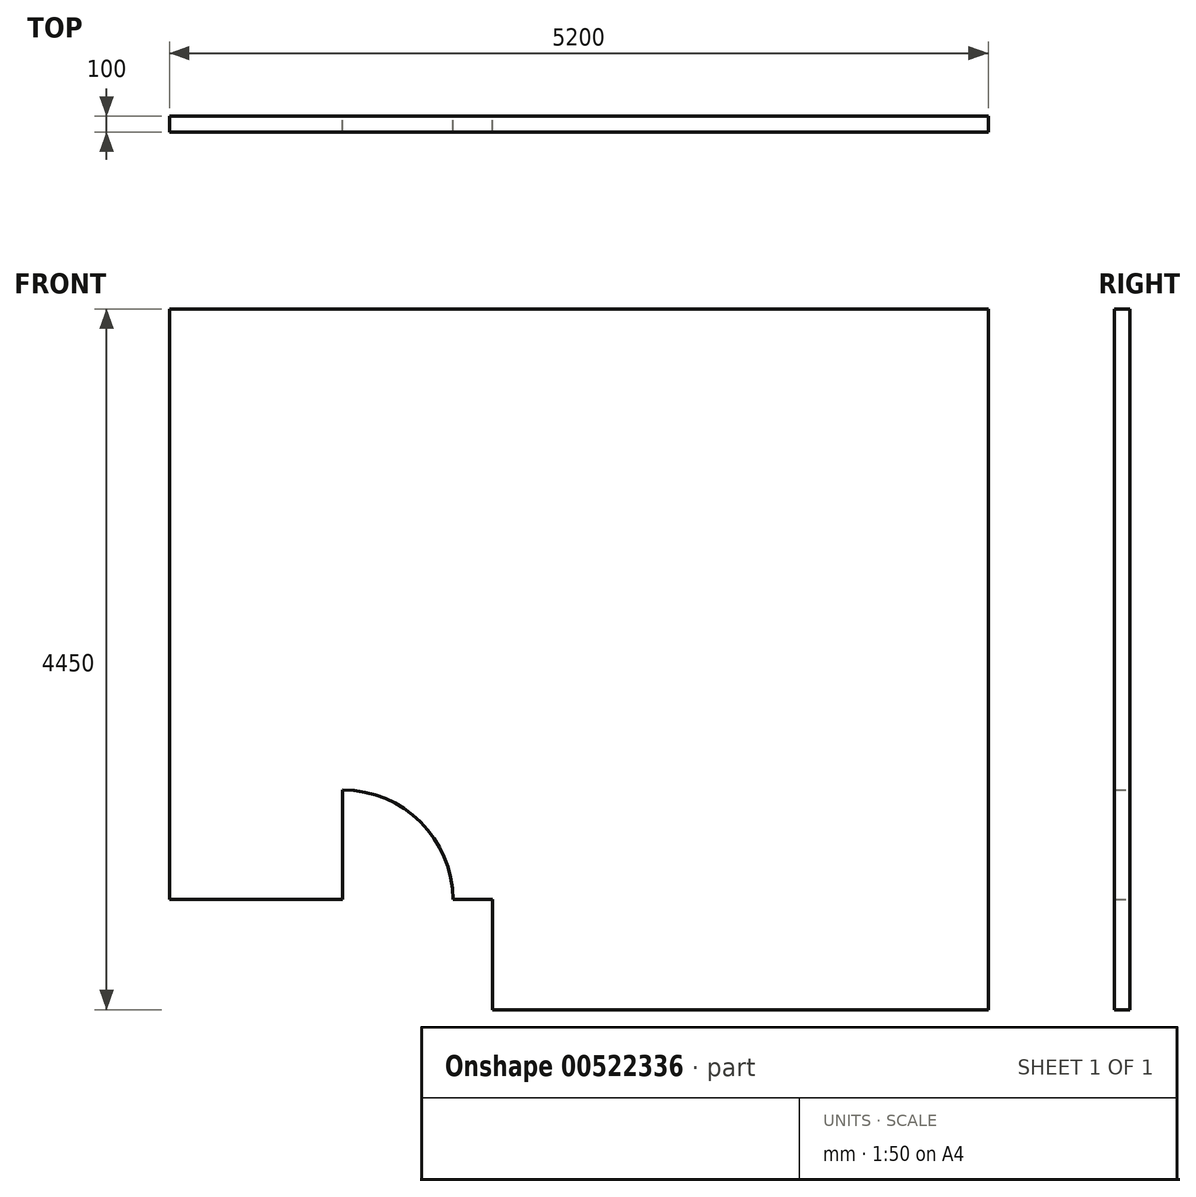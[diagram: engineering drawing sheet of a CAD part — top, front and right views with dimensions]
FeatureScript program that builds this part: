
annotation { "Feature Type Name" : "Feature", "Feature Type Description" : "" }
export const myFeature = defineFeature(function(context is Context, id is Id, definition is map)
    precondition{}
    {
        {
            var Q0;
            Q0=qCreatedBy(makeId("Front.planeOp"),FACE);
            var sketch = newSketch(context, id + "F0", { "sketchPlane" : qUnion([Q0])});
            skLineSegment(sketch, "E0", {"start": v(0, 0) * mm, "end": v(0, 3750) * mm});
            skLineSegment(sketch, "E1", {"start": v(0, 3750) * mm, "end": v(5200, 3750) * mm});
            skLineSegment(sketch, "E2", {"start": v(5200, 3750) * mm, "end": v(5200, -700) * mm});
            skLineSegment(sketch, "E3", {"start": v(5200, -700) * mm, "end": v(2050, -700) * mm});
            skLineSegment(sketch, "E4", {"start": v(2050, -700) * mm, "end": v(2050, 0) * mm});
            skLineSegment(sketch, "E5", {"start": v(0, 0) * mm, "end": v(1100, 0) * mm});
            skLineSegment(sketch, "E6", {"start": v(1100, 0) * mm, "end": v(1100, 695.34) * mm});
            skLineSegment(sketch, "E7", {"start": v(2050, 0) * mm, "end": v(1800, 0) * mm});
            skArc(sketch, "E8", {"start": v(1800, 0) * mm, "mid": v(1593.33, 491.97) * mm, "end": v(1100, 695.34) * mm});
            skSolve(sketch);
        }
        {
            var Q0;
            Q0=makeQuery(id+"F0.imprint","IMPRINT",FACE,{"disambiguationData":[TD([[makeQuery(id+"F0.imprint","IMPRINT",EDGE,{"derivedFrom":sQuery(id+"F0.wireOp",EDGE,"E0")}),-1.0]])]});
            extrude(context, id + "F1", {"entities" : qUnion([Q0]), "depth" : 100 * mm, "offsetDistance" : 25 * mm});
        }
    });
